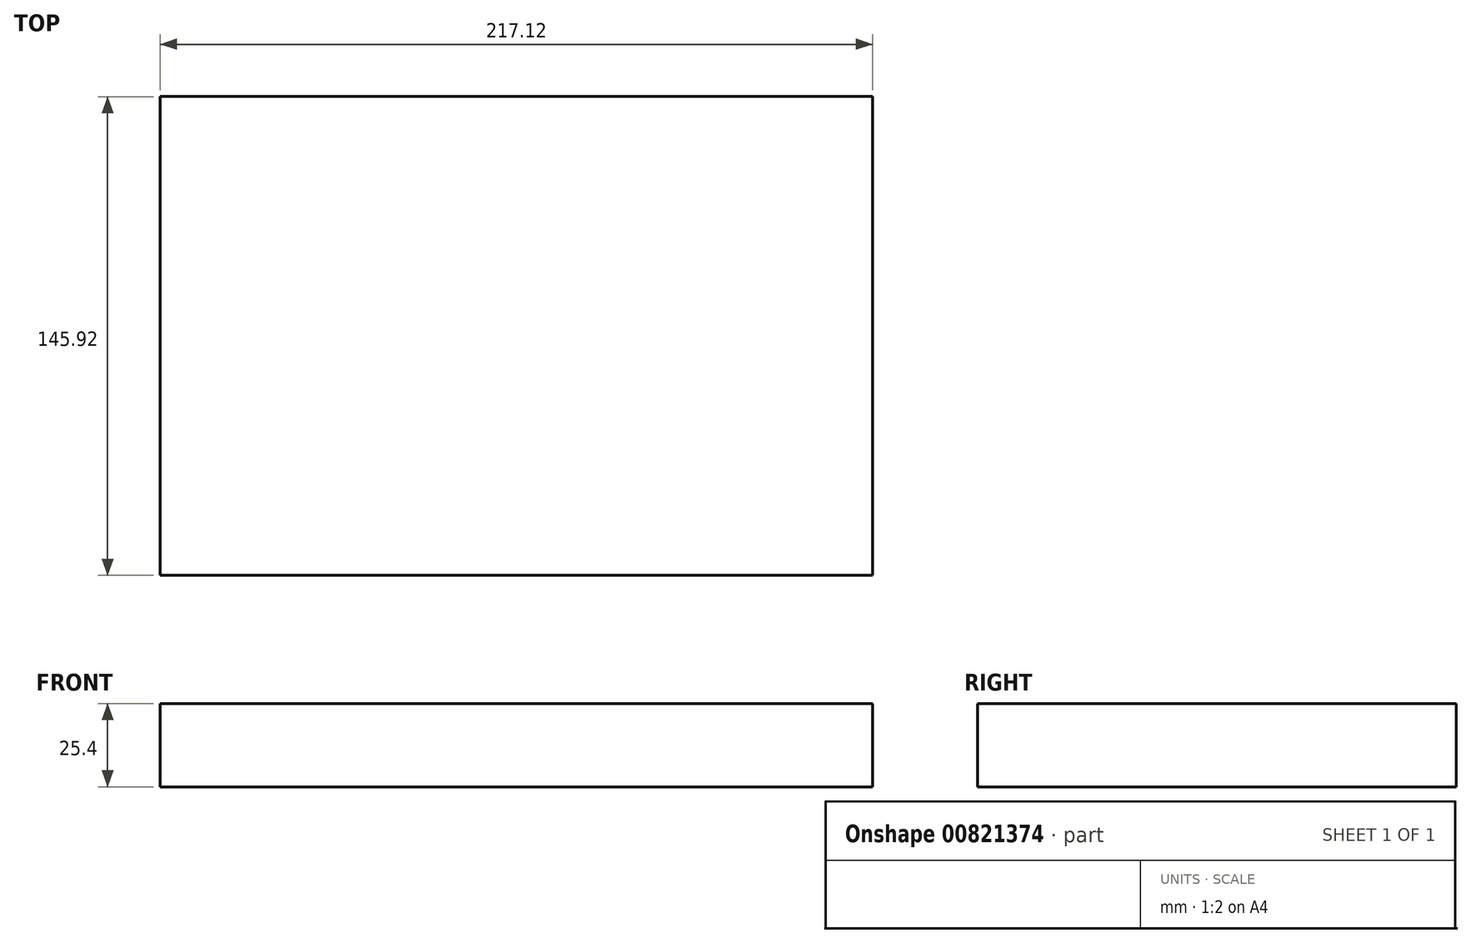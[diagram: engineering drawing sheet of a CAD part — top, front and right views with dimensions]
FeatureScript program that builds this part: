
annotation { "Feature Type Name" : "Feature", "Feature Type Description" : "" }
export const myFeature = defineFeature(function(context is Context, id is Id, definition is map)
    precondition{}
    {
        {
            var Q0;
            Q0=qCreatedBy(makeId("Top.planeOp"),FACE);
            var sketch = newSketch(context, id + "F0", { "sketchPlane" : qUnion([Q0])});
            skLineSegment(sketch, "E0.bottom", {"start": v(-111.4, 77.4) * mm, "end": v(105.72, 77.4) * mm});
            skLineSegment(sketch, "E0.top", {"start": v(-111.4, -68.52) * mm, "end": v(105.72, -68.52) * mm});
            skLineSegment(sketch, "E0.left", {"start": v(-111.4, 77.4) * mm, "end": v(-111.4, -68.52) * mm});
            skLineSegment(sketch, "E0.right", {"start": v(105.72, 77.4) * mm, "end": v(105.72, -68.52) * mm});
            skSolve(sketch);
        }
        {
            var Q0;
            Q0 = qSketchRegion(id + "F0", true);
            extrude(context, id + "F1", {"entities" : qUnion([Q0]), "depth" : 25.4 * mm, "offsetDistance" : 25.4 * mm});
        }
        {
            var Q0;
            Q0=qCreatedBy(makeId("Top.planeOp"),FACE);
            var sketch = newSketch(context, id + "F2", { "sketchPlane" : qUnion([Q0])});
            skLineSegment(sketch, "E1.bottom", {"start": v(-49.8, 48.95) * mm, "end": v(49.41, 48.95) * mm});
            skLineSegment(sketch, "E1.top", {"start": v(-49.8, -48.7) * mm, "end": v(49.41, -48.7) * mm});
            skLineSegment(sketch, "E1.left", {"start": v(-49.8, 48.95) * mm, "end": v(-49.8, -48.7) * mm});
            skLineSegment(sketch, "E1.right", {"start": v(49.41, 48.95) * mm, "end": v(49.41, -48.7) * mm});
            skSolve(sketch);
        }
        {
            var Q0;
            Q0 = qSketchRegion(id + "F2", true);
            extrude(context, id + "F3", {"entities" : qUnion([Q0]), "operationType" : NewBodyOperationType.REMOVE, "oppositeDirection" : true, "depth" : 25 * mm, "offsetDistance" : 25.4 * mm});
        }
    });
